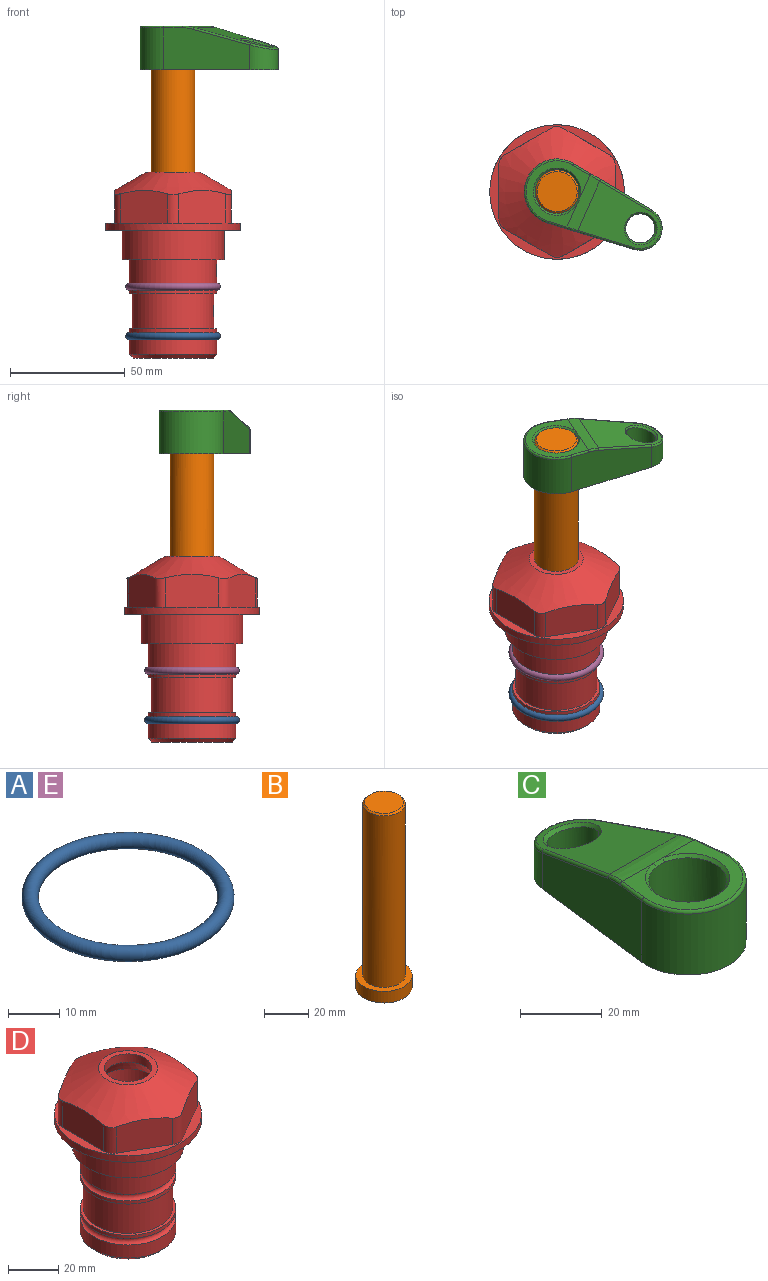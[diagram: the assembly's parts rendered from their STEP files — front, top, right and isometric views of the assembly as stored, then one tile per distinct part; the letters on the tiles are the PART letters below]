
ASSEMBLY  parts=5 mates=4
PART A: 1 faces, bbox 44.7x44.7x3.2 mm
  f0: torus R=19.05mm, axis (0,0,1), area 1193.9mm2
PART B: 6 faces, bbox 25.4x25.4x101.6 mm
  f0: plane 17.46x17.46mm, normal (0,0,1), area 239.5mm2, adj f5
  f1: plane 25.4x25.4mm, normal (0,0,-1), area 506.7mm2, adj f2
  f2: cylinder r=12.7mm len=25.4mm, axis (0,0,1), area 506.7mm2, adj f1,f3
  f3: plane 25.4x25.4mm, normal (0,0,1), area 221.7mm2, adj f2,f4
  f4: cylinder r=9.53mm len=94.46mm, axis (0,0,1), area 5653mm2, adj f3,f5
  f5: cone r=8.73mm half-angle=45deg, axis (0,0,-1), area 64.4mm2, adj f0,f4
PART C: 31 faces, bbox 31.7x65.5x19.8 mm
  f0: plane 39.12x18.26mm, normal (0.99,0.12,0), area 612.2mm2, adj f1,f4,f7,f11,f13,f15
  f1: cylinder r=9.53mm len=18.91mm, axis (0,0,-1), area 296.1mm2, adj f0,f2,f7,f17
  f2: plane 39.12x18.26mm, normal (-0.99,0.12,0), area 612.2mm2, adj f1,f4,f7,f12,f14,f16
  f3: cylinder r=6.35mm len=12.7mm, axis (0,0,-1), area 362.4mm2, adj f7,f18
  f4: cylinder r=14.29mm len=28.58mm, axis (0,0,-1), area 882.2mm2, adj f0,f2,f7,f10
  f5: cylinder r=9.53mm len=19.05mm, axis (0,0,-1), area 1092.6mm2, adj f7,f19,f20
  f6: plane 26.99x23.69mm, normal (0,0,1), area 216.2mm2, adj f9,f10,f11,f12,f19
  f7: plane 63.5x28.58mm, normal (0,0,-1), area 661.8mm2, adj f0,f1,f2,f3,f4,f5,f22,f23
  f8: plane 33.52x23.6mm, normal (0,0.26,0.97), area 486mm2, adj f9,f15,f16,f17,f18
  f9: cylinder r=19.05mm len=24.72mm, axis (1,0,0), area 120.4mm2, adj f6,f8,f13,f14,f20
  f10: torus R=13.49mm, axis (0,0,1), area 59mm2, adj f4,f6,f11,f12
  f11: cylinder r=0.79mm len=8.67mm, axis (0.12,-0.99,0), area 10.8mm2, adj f0,f6,f10,f13
  f12: cylinder r=0.79mm len=8.67mm, axis (0.12,0.99,0), area 10.8mm2, adj f2,f6,f10,f14
  f13: bspline ~4.95x1.42mm, area 6.1mm2, adj f0,f9,f11,f15
  f14: bspline ~4.95x1.42mm, area 6.1mm2, adj f2,f9,f12,f16
  f15: cylinder r=0.79mm len=25.95mm, axis (0.12,-0.96,0.26), area 32.9mm2, adj f0,f8,f13,f17
  f16: cylinder r=0.79mm len=25.95mm, axis (0.12,0.96,-0.26), area 32.9mm2, adj f2,f8,f14,f17
  f17: bspline ~18.91x8.38mm, area 30mm2, adj f1,f8,f15,f16
  f18: bspline ~14.29x14.29mm, area 48.3mm2, adj f3,f8
  f19: cone r=9.53mm half-angle=45deg, axis (0,0,1), area 66.5mm2, adj f5,f6,f20
  f20: bspline ~3.22x0.96mm, area 3.5mm2, adj f5,f9,f19
  f21: plane 2.75x2.72mm, normal (0,0,-1), area 2.9mm2, adj f23,f25,f28
  f22: plane 23.05x15.88mm, normal (-0.99,-0.12,0), area 323.6mm2, adj f7,f25,f26,f27,f28,f29
  f23: plane 23.05x15.88mm, normal (0.99,-0.12,0), area 323.6mm2, adj f7,f21,f25,f27,f28,f30
  f24: cylinder r=9.53mm len=10.69mm, axis (0,0,-1), area 114.7mm2, adj f7,f27,f29,f30
  f25: cylinder r=12.7mm len=20.59mm, axis (0,0,-1), area 381.1mm2, adj f7,f21,f22,f23,f26,f28
  f26: plane 2.75x2.72mm, normal (0,0,-1), area 2.9mm2, adj f22,f25,f28
  f27: plane 19.72x18.37mm, normal (0,-0.26,-0.97), area 291.8mm2, adj f22,f23,f24,f28,f29,f30
  f28: cylinder r=15.88mm len=19.92mm, axis (1,0,0), area 54.8mm2, adj f21,f22,f23,f25,f26,f27
  f29: cylinder r=1.59mm len=11mm, axis (0,0,-1), area 34.7mm2, adj f7,f22,f24,f27
  f30: cylinder r=1.59mm len=11mm, axis (0,0,-1), area 34.7mm2, adj f7,f23,f24,f27
PART D: 36 faces, bbox 58.7x58.7x81 mm
  f0: cylinder r=17.78mm len=35.56mm, axis (0,0,1), area 1670.8mm2, adj f23,f24,f31
  f1: cylinder r=19.05mm len=38.1mm, axis (0,0,1), area 1191.9mm2, adj f26,f27,f30
  f2: plane 58.66x58.66mm, normal (0,0,-1), area 1150.6mm2, adj f3,f28
  f3: cylinder r=29.33mm len=58.66mm, axis (0,0,-1), area 585.1mm2, adj f2,f4
  f4: plane 58.66x58.66mm, normal (0,0,1), area 475.9mm2, adj f3,f5,f6,f7,f8,f9,f10,f11
  f5: plane 20.32x14.34mm, normal (-0.5,0.87,0), area 324.4mm2, adj f4,f15,f16,f17
  f6: plane 20.32x14.34mm, normal (0.5,0.87,0), area 324.4mm2, adj f4,f14,f15,f17
  f7: plane 23.48x14.34mm, normal (1,0,0), area 324.4mm2, adj f4,f13,f14,f17
  f8: plane 20.32x14.34mm, normal (0.5,-0.87,0), area 324.4mm2, adj f4,f12,f13,f17
  f9: plane 20.32x14.34mm, normal (-0.5,-0.87,0), area 324.4mm2, adj f4,f11,f12,f17
  f10: plane 23.48x14.34mm, normal (-1,0,0), area 324.4mm2, adj f4,f11,f16,f17
  f11: cylinder r=5.08mm len=12.85mm, axis (0,0,-1), area 67.2mm2, adj f4,f9,f10,f17
  f12: cylinder r=5.08mm len=12.85mm, axis (0,0,-1), area 67.2mm2, adj f4,f8,f9,f17
  f13: cylinder r=5.08mm len=12.85mm, axis (0,0,-1), area 67.2mm2, adj f4,f7,f8,f17
  f14: cylinder r=5.08mm len=12.85mm, axis (0,0,-1), area 67.2mm2, adj f4,f6,f7,f17
  f15: cylinder r=5.08mm len=12.85mm, axis (0,0,-1), area 67.2mm2, adj f4,f5,f6,f17
  f16: cylinder r=5.08mm len=12.85mm, axis (0,0,-1), area 67.2mm2, adj f4,f5,f10,f17
  f17: cone r=11.73mm half-angle=60deg, axis (0,0,-1), area 2071.8mm2, adj f5,f6,f7,f8,f9,f10,f11,f12
  f18: plane 23.46x23.46mm, normal (0,0,1), area 147.4mm2, adj f17,f35
  f19: plane 34.93x34.93mm, normal (0,0,-1), area 958mm2, adj f29
  f20: cylinder r=19.05mm len=38.1mm, axis (0,0,1), area 760.1mm2, adj f21,f29
  f21: torus R=19.05mm, axis (0,0,1), area 565.3mm2, adj f20,f22
  f22: cylinder r=19.05mm len=38.1mm, axis (0,0,1), area 190mm2, adj f21,f23
  f23: plane 38.1x38.1mm, normal (0,0,1), area 146.9mm2, adj f0,f22
  f24: plane 38.1x38.1mm, normal (0,0,-1), area 146.9mm2, adj f0,f25
  f25: cylinder r=19.05mm len=38.1mm, axis (0,0,1), area 190mm2, adj f24,f26
  f26: torus R=19.05mm, axis (0,0,1), area 565.3mm2, adj f1,f25
  f27: plane 44.45x44.45mm, normal (0,0,-1), area 411.7mm2, adj f1,f28
  f28: cylinder r=22.23mm len=44.45mm, axis (0,0,1), area 1773.5mm2, adj f2,f27
  f29: cone r=19.05mm half-angle=45deg, axis (0,0,1), area 257.5mm2, adj f19,f20
  f30: cylinder r=3.17mm len=6.75mm, axis (-1,0,0), area 128mm2, adj f1,f33
  f31: cylinder r=3.17mm len=6.35mm, axis (-1,0,0), area 102.5mm2, adj f0,f33
  f32: plane 25.4x25.4mm, normal (0,0,1), area 506.7mm2, adj f33
  f33: cylinder r=12.7mm len=66.42mm, axis (0,0,-1), area 5236.2mm2, adj f30,f31,f32,f34
  f34: cone r=9.53mm half-angle=30deg, axis (0,0,-1), area 443.4mm2, adj f33,f35
  f35: cylinder r=9.53mm len=19.05mm, axis (0,0,-1), area 240.9mm2, adj f18,f34
PART E: same geometry as A
PLACE A t=(0,0,-21.59)mm
PLACE B rot(axis=(0,0,-1),113.8deg) t=(0,0,25.71)mm
PLACE C rot(axis=(0,0,-1),113.8deg) t=(0,0,25.71)mm
PLACE D at identity fixed
PLACE E at identity
MATE cylindrical B.f2 <-> D.f0  axis (0,0,-1) through (0,0,-12.39)mm
MATE fastened A.f0 <-> D.f0  axis (0,0,1) through (0,0,-46.1)mm
MATE fastened B.f2 <-> C.f4  axis (0,0,1) through (0,0,89.21)mm
MATE fastened E.f0 <-> D.f0  axis (0,0,1) through (0,0,-24.51)mm
